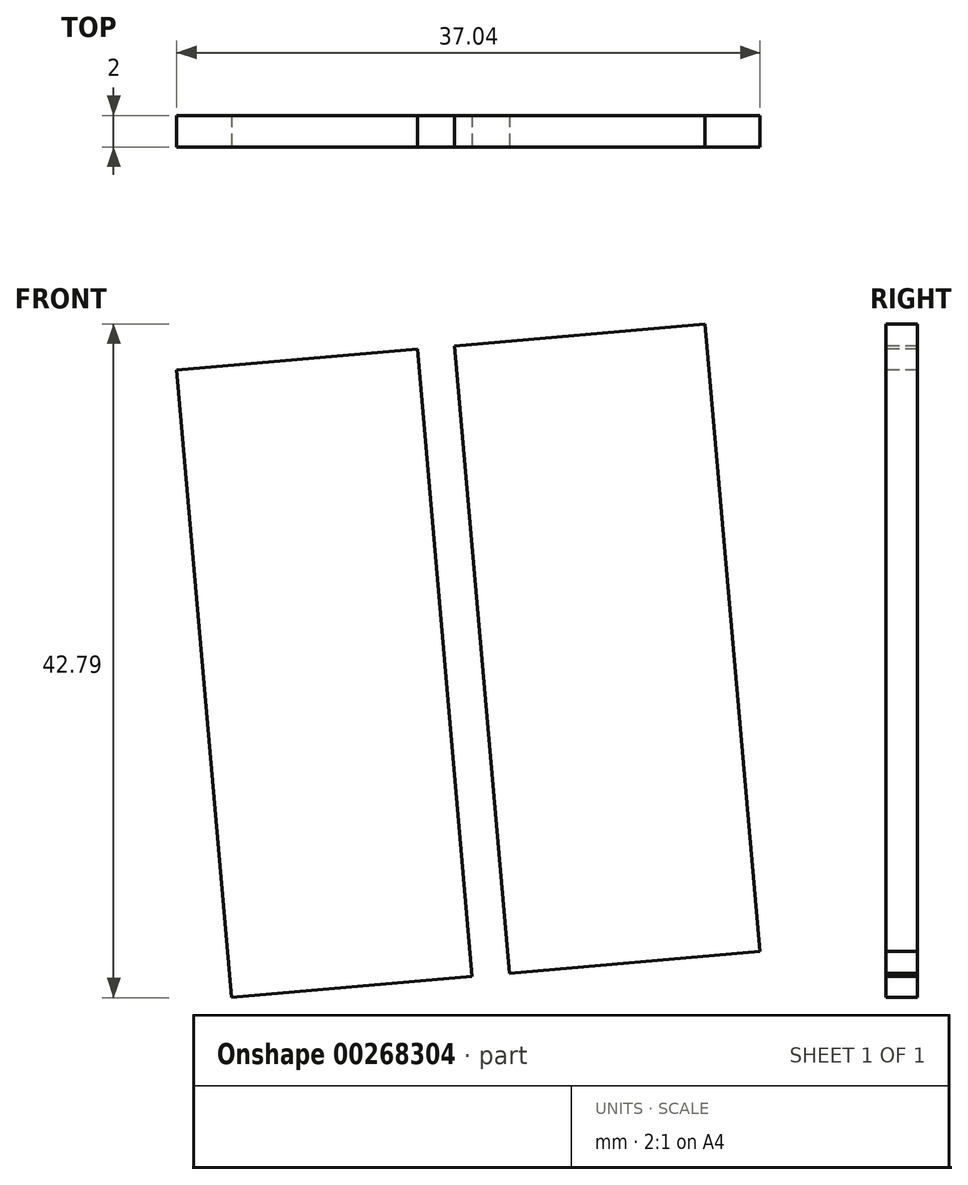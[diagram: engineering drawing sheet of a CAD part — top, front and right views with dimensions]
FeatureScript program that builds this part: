
annotation { "Feature Type Name" : "Feature", "Feature Type Description" : "" }
export const myFeature = defineFeature(function(context is Context, id is Id, definition is map)
    precondition{}
    {
        {
            var Q0;
            Q0=qCreatedBy(makeId("Top.planeOp"),FACE);
            var sketch = newSketch(context, id + "F0", { "sketchPlane" : qUnion([Q0])});
            skLineSegment(sketch, "E0.bottom", {"start": v(-16.71, 1) * mm, "end": v(-1.5, 1) * mm});
            skLineSegment(sketch, "E0.top", {"start": v(-16.71, -1) * mm, "end": v(-1.5, -1) * mm});
            skLineSegment(sketch, "E0.left", {"start": v(-16.71, 1) * mm, "end": v(-16.71, -1) * mm});
            skLineSegment(sketch, "E0.right", {"start": v(-1.5, 1) * mm, "end": v(-1.5, -1) * mm});
            skLineSegment(sketch, "E1.bottom", {"start": v(1, 1) * mm, "end": v(16.97, 1) * mm});
            skLineSegment(sketch, "E1.top", {"start": v(1, -1) * mm, "end": v(16.97, -1) * mm});
            skLineSegment(sketch, "E1.left", {"start": v(1, 1) * mm, "end": v(1, -1) * mm});
            skLineSegment(sketch, "E1.right", {"start": v(16.97, 1) * mm, "end": v(16.97, -1) * mm});
            skLineSegment(sketch, "E2.bottom", {"start": v(-16.71, 1) * mm, "end": v(-1.38, 1) * mm});
            skLineSegment(sketch, "E2.top", {"start": v(-16.71, -1) * mm, "end": v(-1.38, -1) * mm});
            skLineSegment(sketch, "E2.right", {"start": v(-1.38, 1) * mm, "end": v(-1.38, -1) * mm});
            skLineSegment(sketch, "E3.bottom", {"start": v(2.62, 1) * mm, "end": v(16.97, 1) * mm});
            skLineSegment(sketch, "E3.top", {"start": v(2.62, -1) * mm, "end": v(16.97, -1) * mm});
            skLineSegment(sketch, "E3.left", {"start": v(2.62, 1) * mm, "end": v(2.62, -1) * mm});
            skSolve(sketch);
        }
        {
            var Q0;
            Q0 = qSketchRegion(id + "F0", true);
            extrude(context, id + "F1", {"entities" : qUnion([Q0]), "depth" : 40 * mm});
        }
        {
            var Q0;
            Q0=makeQuery(id+"F1.opExtrude","SWEPT_BODY",BODY,{"disambiguationData":[OSD([sQuery(id+"F0.wireOp",EDGE,"E2.bottom"),sQuery(id+"F0.wireOp",EDGE,"E2.top"),sQuery(id+"F0.wireOp",EDGE,"E0.left"),sQuery(id+"F0.wireOp",EDGE,"E2.right")])]});
            var Q1;
            Q1=makeQuery(id+"F1.opExtrude","SWEPT_BODY",BODY,{"disambiguationData":[OSD([sQuery(id+"F0.wireOp",EDGE,"E3.bottom"),sQuery(id+"F0.wireOp",EDGE,"E3.top"),sQuery(id+"F0.wireOp",EDGE,"E3.left"),sQuery(id+"F0.wireOp",EDGE,"E1.right")])]});
            var Q2;
            Q2=makeQuery(id+"F1.opExtrude","CAP_EDGE",EDGE,{"disambiguationData":[OSD([sQuery(id+"F0.wireOp",EDGE,"E1.right")])],"isStart":true});
            transform(context, id + "F2", {"entities" : qUnion([Q0, Q1]), "transformType" : TransformType.ROTATION, "transformAxis" : qUnion([Q2]), "angle" : 5 * degree, "makeCopy" : false});
        }
    });
